# Revit family: QF_MACOM_HOSDBxxx-2M
name_source: partatom
category: Equipamento especial
units: mm (PartAtom-declared; Revit-internal decimal feet)

## family parameters
Com base no plano de trabalho = Não
Compartilhado = Não
Corte com vazios quando carregada = Não
Cota do conector redondo = Utilizar diâmetro
Número OmniClass = 23.40.40.14.27
Ponto de cálculo do ambiente = Não
Sempre na vertical = Sim
Tipo de parte = Normal
Título OmniClass = Ice Machines

## types (2) — shared parameters
Base Height = 152,00 mm
Conn Conduit = Sim
Cycle = 60 Hz
Depth = 782,00 mm
Elec Conn Connection Height = 1260,00 mm
Elevação padrão = 0,00 mm
FL Amps = 1 A
Fabricante = MACOM
Height = 1349,00 mm
Indirect Waste Size = 1"
Legs 1 = Sim
Legs 2 = Não
Max Overcurrent Protection = 0 A
Min Ckt Ampacity = 0 A
Phase = 1
Show Clearance = Sim
Volts = 220 V
Weight = 0,00 kg

## per-type parameters (varying)
| type | Capacity | D1 | Descrição | Length | Volume |
| HOSDB200-2M | 90,00 kg | 95,25 mm | DISPENSER DE GELO HOSHIZAKI, CAPACIDADE 90KG - 220V MONOF-762X762X1346 | 762,00 mm | 0,80 m³ |
| HOSDB130-2M | 59,00 kg | 44,45 mm | DISPENSER DE GELO HOSHIZAKI, CAPACIDADE 59KG - 220V MONOF-560X762X1346 | 560,00 mm | 0,59 m³ |

note: column(s) folded — value = type name in every type: Modelo

## geometry (parser evidence)
native form markers: Blend x4, Sweep x6
no freeform markers — native parametric forms only
